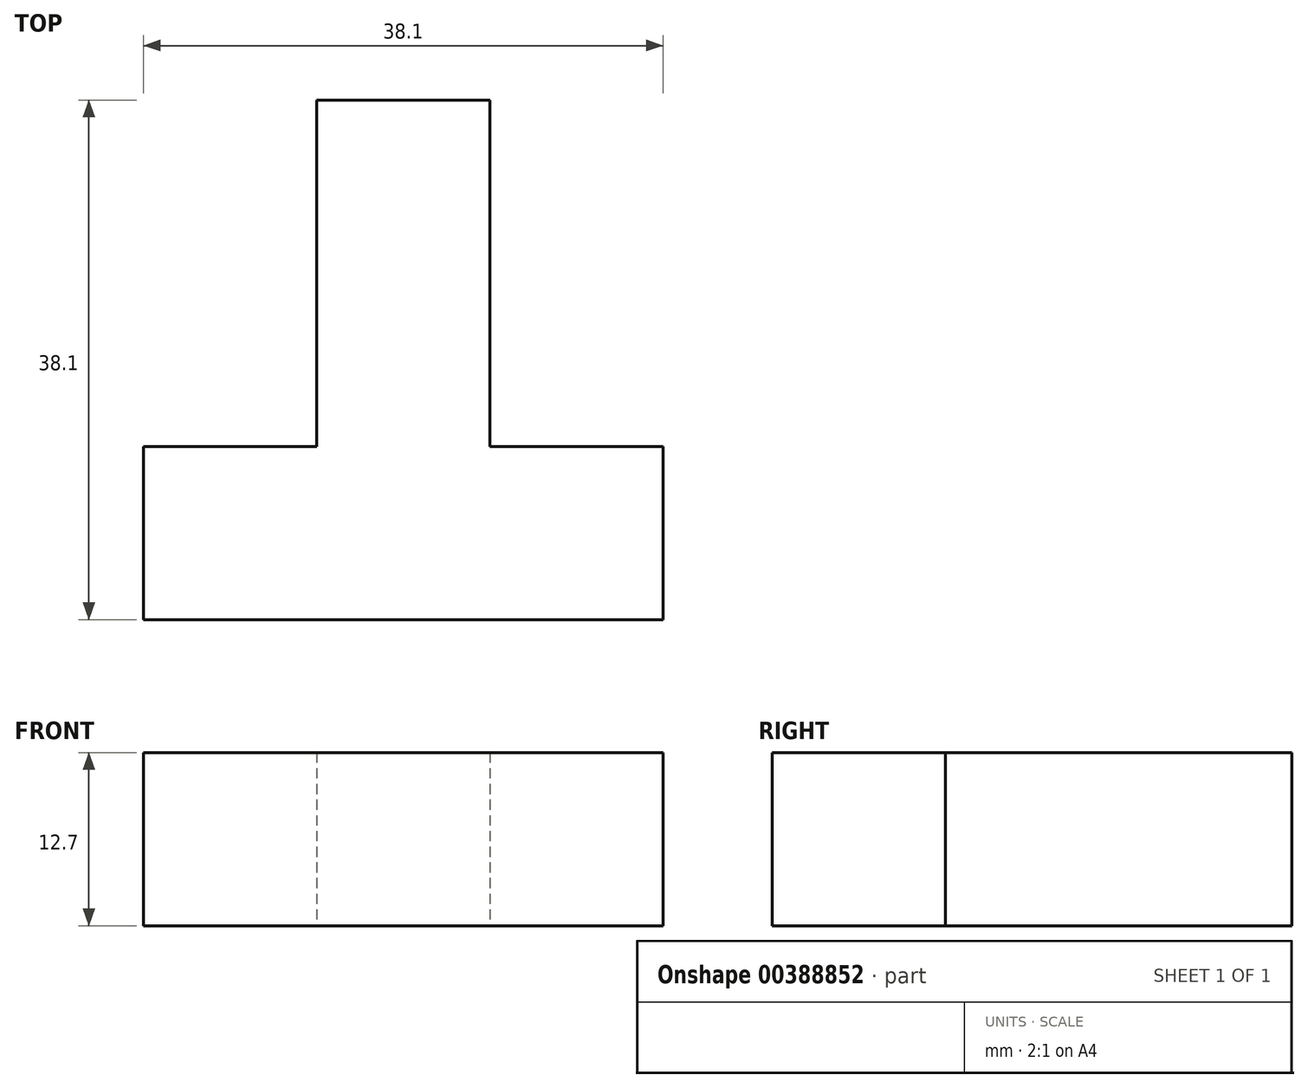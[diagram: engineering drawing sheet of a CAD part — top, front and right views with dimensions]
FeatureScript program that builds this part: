
annotation { "Feature Type Name" : "Feature", "Feature Type Description" : "" }
export const myFeature = defineFeature(function(context is Context, id is Id, definition is map)
    precondition{}
    {
        {
            var Q0;
            Q0=qCreatedBy(makeId("Top.planeOp"),FACE);
            var sketch = newSketch(context, id + "F0", { "sketchPlane" : qUnion([Q0])});
            skLineSegment(sketch, "E0.bottom", {"start": v(0, 0) * mm, "end": v(12.7, 0) * mm});
            skLineSegment(sketch, "E0.top", {"start": v(0, 38.1) * mm, "end": v(12.7, 38.1) * mm});
            skLineSegment(sketch, "E0.left", {"start": v(0, 12.7) * mm, "end": v(0, 38.1) * mm});
            skLineSegment(sketch, "E0.right", {"start": v(12.7, 12.7) * mm, "end": v(12.7, 38.1) * mm});
            skLineSegment(sketch, "E1.bottom", {"start": v(12.7, 0) * mm, "end": v(25.4, 0) * mm});
            skLineSegment(sketch, "E1.top", {"start": v(12.7, 12.7) * mm, "end": v(25.4, 12.7) * mm});
            skLineSegment(sketch, "E1.right", {"start": v(25.4, 0) * mm, "end": v(25.4, 12.7) * mm});
            skLineSegment(sketch, "E2.bottom", {"start": v(0, 0) * mm, "end": v(-12.7, 0) * mm});
            skLineSegment(sketch, "E2.top", {"start": v(0, 12.7) * mm, "end": v(-12.7, 12.7) * mm});
            skLineSegment(sketch, "E2.right", {"start": v(-12.7, 0) * mm, "end": v(-12.7, 12.7) * mm});
            skSolve(sketch);
        }
        {
            var Q0;
            Q0=makeQuery(id+"F0.imprint","IMPRINT",FACE,{"disambiguationData":[TD([[makeQuery(id+"F0.imprint","IMPRINT",EDGE,{"derivedFrom":sQuery(id+"F0.wireOp",EDGE,"E0.bottom")}),1.0]])]});
            extrude(context, id + "F1", {"entities" : qUnion([Q0]), "depth" : 12.7 * mm});
        }
    });
